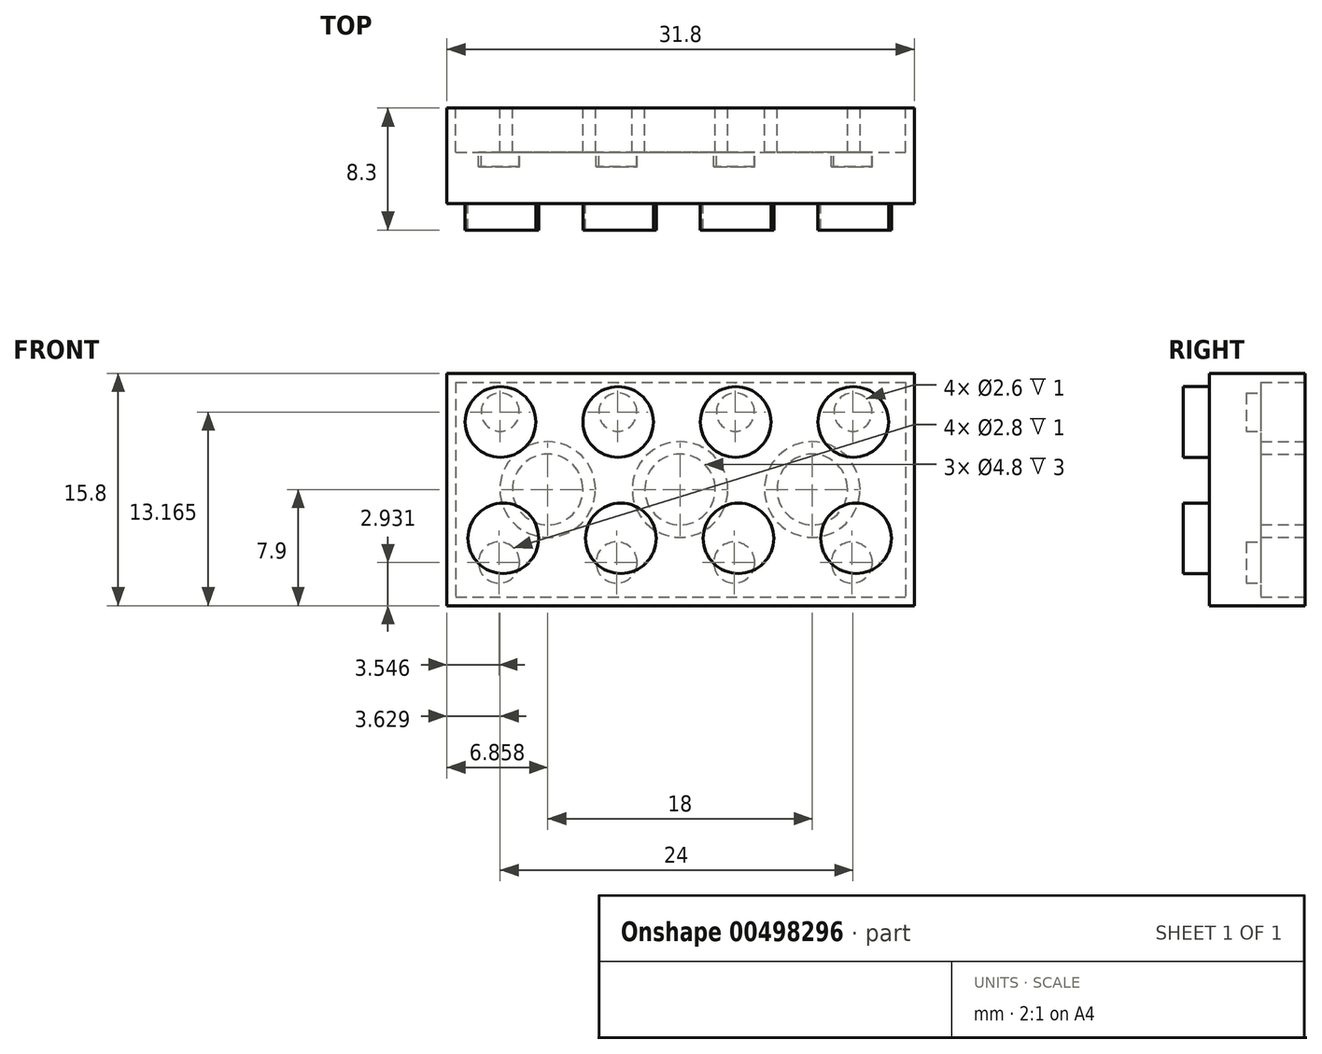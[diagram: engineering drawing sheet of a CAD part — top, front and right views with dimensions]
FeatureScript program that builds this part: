
annotation { "Feature Type Name" : "Feature", "Feature Type Description" : "" }
export const myFeature = defineFeature(function(context is Context, id is Id, definition is map)
    precondition{}
    {
        {
            var Q0;
            Q0=qCreatedBy(makeId("Front.planeOp"),FACE);
            var sketch = newSketch(context, id + "F0", { "sketchPlane" : qUnion([Q0])});
            skLineSegment(sketch, "E0.bottom", {"start": v(15.9, 7.9) * mm, "end": v(-15.9, 7.9) * mm});
            skLineSegment(sketch, "E0.top", {"start": v(15.9, -7.9) * mm, "end": v(-15.9, -7.9) * mm});
            skLineSegment(sketch, "E0.left", {"start": v(15.9, 7.9) * mm, "end": v(15.9, -7.9) * mm});
            skLineSegment(sketch, "E0.right", {"start": v(-15.9, 7.9) * mm, "end": v(-15.9, -7.9) * mm});
            skPoint(sketch, "E0.middle", {"position": v(0, 0) * mm});
            skSolve(sketch);
        }
        {
            var Q0;
            Q0 = qSketchRegion(id + "F0", true);
            extrude(context, id + "F1", {"entities" : qUnion([Q0]), "depth" : 6.5 * mm});
        }
        {
            var Q0;
            Q0=makeQuery(id+"F1.opExtrude","CAP_FACE",FACE,{"disambiguationData":[OSD([sQuery(id+"F0.wireOp",EDGE,"E0.bottom"),sQuery(id+"F0.wireOp",EDGE,"E0.top"),sQuery(id+"F0.wireOp",EDGE,"E0.left"),sQuery(id+"F0.wireOp",EDGE,"E0.right")])],"isStart":false});
            var sketch = newSketch(context, id + "F2", { "sketchPlane" : qUnion([Q0])});
            skCircle(sketch, "E1", {"center": v(-12.25, 4.6) * mm, "radius": 2.4 * mm});
            skCircle(sketch, "E2.1.0.0", {"center": v(-4.25, 4.6) * mm, "radius": 2.4 * mm});
            skCircle(sketch, "E2.2.0.0", {"center": v(3.75, 4.6) * mm, "radius": 2.4 * mm});
            skCircle(sketch, "E2.3.0.0", {"center": v(11.75, 4.6) * mm, "radius": 2.4 * mm});
            skLineSegment(sketch, "E2.direction1", {"start": v(-12.25, 4.6) * mm, "end": v(-4.25, 4.6) * mm, "construction": true});
            skSolve(sketch);
        }
        {
            var Q0;
            Q0=makeQuery(id+"F2.imprint","IMPRINT",FACE,{"disambiguationData":[TD([[makeQuery(id+"F2.imprint","IMPRINT",EDGE,{"derivedFrom":sQuery(id+"F2.wireOp",EDGE,"E1")}),-1.0]])]});
            var sketch = newSketch(context, id + "F3", { "sketchPlane" : qUnion([Q0])});
            skCircle(sketch, "E3", {"center": v(-12.06, -3.32) * mm, "radius": 2.4 * mm});
            skCircle(sketch, "E4.1.0.0", {"center": v(-4.06, -3.32) * mm, "radius": 2.4 * mm});
            skCircle(sketch, "E4.2.0.0", {"center": v(3.94, -3.32) * mm, "radius": 2.4 * mm});
            skCircle(sketch, "E4.3.0.0", {"center": v(11.94, -3.32) * mm, "radius": 2.4 * mm});
            skLineSegment(sketch, "E4.direction1", {"start": v(-12.06, -3.32) * mm, "end": v(-4.06, -3.32) * mm, "construction": true});
            skSolve(sketch);
        }
        {
            var Q0;
            Q0 = qSketchRegion(id + "F3", true);
            extrude(context, id + "F4", {"entities" : qUnion([Q0]), "operationType" : NewBodyOperationType.ADD, "depth" : 1.8 * mm});
        }
        {
            var Q0;
            Q0 = qSketchRegion(id + "F2", true);
            extrude(context, id + "F5", {"entities" : qUnion([Q0]), "operationType" : NewBodyOperationType.ADD, "depth" : 1.8 * mm});
        }
        {
            var Q0;
            Q0=makeQuery(id+"F1.opExtrude","CAP_FACE",FACE,{"disambiguationData":[OSD([sQuery(id+"F0.wireOp",EDGE,"E0.bottom"),sQuery(id+"F0.wireOp",EDGE,"E0.top"),sQuery(id+"F0.wireOp",EDGE,"E0.left"),sQuery(id+"F0.wireOp",EDGE,"E0.right")])],"isStart":true});
            var sketch = newSketch(context, id + "F6", { "sketchPlane" : qUnion([Q0])});
            skCircle(sketch, "E5", {"center": v(-8.96, 0) * mm, "radius": 2.4 * mm});
            skCircle(sketch, "E6", {"center": v(-8.96, 0) * mm, "radius": 3.25 * mm});
            skCircle(sketch, "E7.1.0.0", {"center": v(0.04, 0) * mm, "radius": 3.25 * mm});
            skCircle(sketch, "E7.1.0.1", {"center": v(0.04, 0) * mm, "radius": 2.4 * mm});
            skCircle(sketch, "E7.2.0.0", {"center": v(9.04, 0) * mm, "radius": 3.25 * mm});
            skCircle(sketch, "E7.2.0.1", {"center": v(9.04, 0) * mm, "radius": 2.4 * mm});
            skLineSegment(sketch, "E7.direction1", {"start": v(-8.96, 0) * mm, "end": v(0.04, 0) * mm, "construction": true});
            skLineSegment(sketch, "E8.bottom", {"start": v(15.3, 7.3) * mm, "end": v(-15.3, 7.3) * mm});
            skLineSegment(sketch, "E8.top", {"start": v(15.3, -7.3) * mm, "end": v(-15.3, -7.3) * mm});
            skLineSegment(sketch, "E8.left", {"start": v(15.3, 7.3) * mm, "end": v(15.3, -7.3) * mm});
            skLineSegment(sketch, "E8.right", {"start": v(-15.3, 7.3) * mm, "end": v(-15.3, -7.3) * mm});
            skPoint(sketch, "E8.middle", {"position": v(0, 0) * mm});
            skSolve(sketch);
        }
        {
            var Q0;
            Q0=makeQuery(id+"F6.imprint","IMPRINT",FACE,{"disambiguationData":[TD([[makeQuery(id+"F6.imprint","IMPRINT",EDGE,{"derivedFrom":sQuery(id+"F6.wireOp",EDGE,"E6")}),-1.0]])]});
            var Q1;
            Q1=makeQuery(id+"F6.imprint","IMPRINT",FACE,{"disambiguationData":[TD([[makeQuery(id+"F6.imprint","IMPRINT",EDGE,{"derivedFrom":sQuery(id+"F6.wireOp",EDGE,"E5")}),1.0]])]});
            var Q2;
            Q2=makeQuery(id+"F6.imprint","IMPRINT",FACE,{"disambiguationData":[TD([[makeQuery(id+"F6.imprint","IMPRINT",EDGE,{"derivedFrom":sQuery(id+"F6.wireOp",EDGE,"E7.1.0.1")}),1.0]])]});
            var Q3;
            Q3=makeQuery(id+"F6.imprint","IMPRINT",FACE,{"disambiguationData":[TD([[makeQuery(id+"F6.imprint","IMPRINT",EDGE,{"derivedFrom":sQuery(id+"F6.wireOp",EDGE,"E7.2.0.1")}),1.0]])]});
            extrude(context, id + "F7", {"entities" : qUnion([Q0, Q1, Q2, Q3]), "operationType" : NewBodyOperationType.REMOVE, "oppositeDirection" : true, "depth" : 3 * mm});
        }
        {
            var Q0;
            Q0=makeQuery(id+"F7.boolean.opBoolean","COPY",FACE,{"derivedFrom":makeQuery(id+"F7.opExtrude","CAP_FACE",FACE,{"disambiguationData":[OSD([sQuery(id+"F6.wireOp",EDGE,"E6"),sQuery(id+"F6.wireOp",EDGE,"E7.1.0.0"),sQuery(id+"F6.wireOp",EDGE,"E7.2.0.0"),sQuery(id+"F6.wireOp",EDGE,"E8.bottom"),sQuery(id+"F6.wireOp",EDGE,"E8.top"),sQuery(id+"F6.wireOp",EDGE,"E8.left"),sQuery(id+"F6.wireOp",EDGE,"E8.right")])],"isStart":false})});
            var sketch = newSketch(context, id + "F8", { "sketchPlane" : qUnion([Q0])});
            skCircle(sketch, "E9", {"center": v(-11.73, 5.26) * mm, "radius": 1.3 * mm});
            skCircle(sketch, "E10.1.0.0", {"center": v(-3.73, 5.26) * mm, "radius": 1.3 * mm});
            skCircle(sketch, "E10.2.0.0", {"center": v(4.27, 5.26) * mm, "radius": 1.3 * mm});
            skCircle(sketch, "E10.3.0.0", {"center": v(12.27, 5.26) * mm, "radius": 1.3 * mm});
            skLineSegment(sketch, "E10.direction1", {"start": v(-11.73, 5.26) * mm, "end": v(-3.73, 5.26) * mm, "construction": true});
            skSolve(sketch);
        }
        {
            var Q0;
            Q0=makeQuery(id+"F8.imprint","IMPRINT",FACE,{"disambiguationData":[TD([[makeQuery(id+"F8.imprint","IMPRINT",EDGE,{"derivedFrom":sQuery(id+"F8.wireOp",EDGE,"E9")}),1.0]])]});
            var Q1;
            Q1=makeQuery(id+"F8.imprint","IMPRINT",FACE,{"disambiguationData":[TD([[makeQuery(id+"F8.imprint","IMPRINT",EDGE,{"derivedFrom":sQuery(id+"F8.wireOp",EDGE,"E10.1.0.0")}),1.0]])]});
            var Q2;
            Q2=makeQuery(id+"F8.imprint","IMPRINT",FACE,{"disambiguationData":[TD([[makeQuery(id+"F8.imprint","IMPRINT",EDGE,{"derivedFrom":sQuery(id+"F8.wireOp",EDGE,"E10.2.0.0")}),1.0]])]});
            var Q3;
            Q3=makeQuery(id+"F8.imprint","IMPRINT",FACE,{"disambiguationData":[TD([[makeQuery(id+"F8.imprint","IMPRINT",EDGE,{"derivedFrom":sQuery(id+"F8.wireOp",EDGE,"E10.3.0.0")}),1.0]])]});
            extrude(context, id + "F9", {"entities" : qUnion([Q0, Q1, Q2, Q3]), "operationType" : NewBodyOperationType.REMOVE, "oppositeDirection" : true, "depth" : 1 * mm});
        }
        {
            var Q0;
            Q0=makeQuery(id+"F7.boolean.opBoolean","COPY",FACE,{"derivedFrom":makeQuery(id+"F7.opExtrude","CAP_FACE",FACE,{"disambiguationData":[OSD([sQuery(id+"F6.wireOp",EDGE,"E6"),sQuery(id+"F6.wireOp",EDGE,"E7.1.0.0"),sQuery(id+"F6.wireOp",EDGE,"E7.2.0.0"),sQuery(id+"F6.wireOp",EDGE,"E8.bottom"),sQuery(id+"F6.wireOp",EDGE,"E8.top"),sQuery(id+"F6.wireOp",EDGE,"E8.left"),sQuery(id+"F6.wireOp",EDGE,"E8.right")])],"isStart":false})});
            var sketch = newSketch(context, id + "F10", { "sketchPlane" : qUnion([Q0])});
            skCircle(sketch, "E11", {"center": v(-11.65, -4.97) * mm, "radius": 1.4 * mm});
            skCircle(sketch, "E12.1.0.0", {"center": v(-3.65, -4.97) * mm, "radius": 1.4 * mm});
            skCircle(sketch, "E12.2.0.0", {"center": v(4.35, -4.97) * mm, "radius": 1.4 * mm});
            skCircle(sketch, "E12.3.0.0", {"center": v(12.35, -4.97) * mm, "radius": 1.4 * mm});
            skLineSegment(sketch, "E12.direction1", {"start": v(-11.65, -4.97) * mm, "end": v(-3.65, -4.97) * mm, "construction": true});
            skSolve(sketch);
        }
        {
            var Q0;
            Q0 = qSketchRegion(id + "F10", true);
            extrude(context, id + "F11", {"entities" : qUnion([Q0]), "operationType" : NewBodyOperationType.REMOVE, "oppositeDirection" : true, "depth" : 1 * mm});
        }
    });
